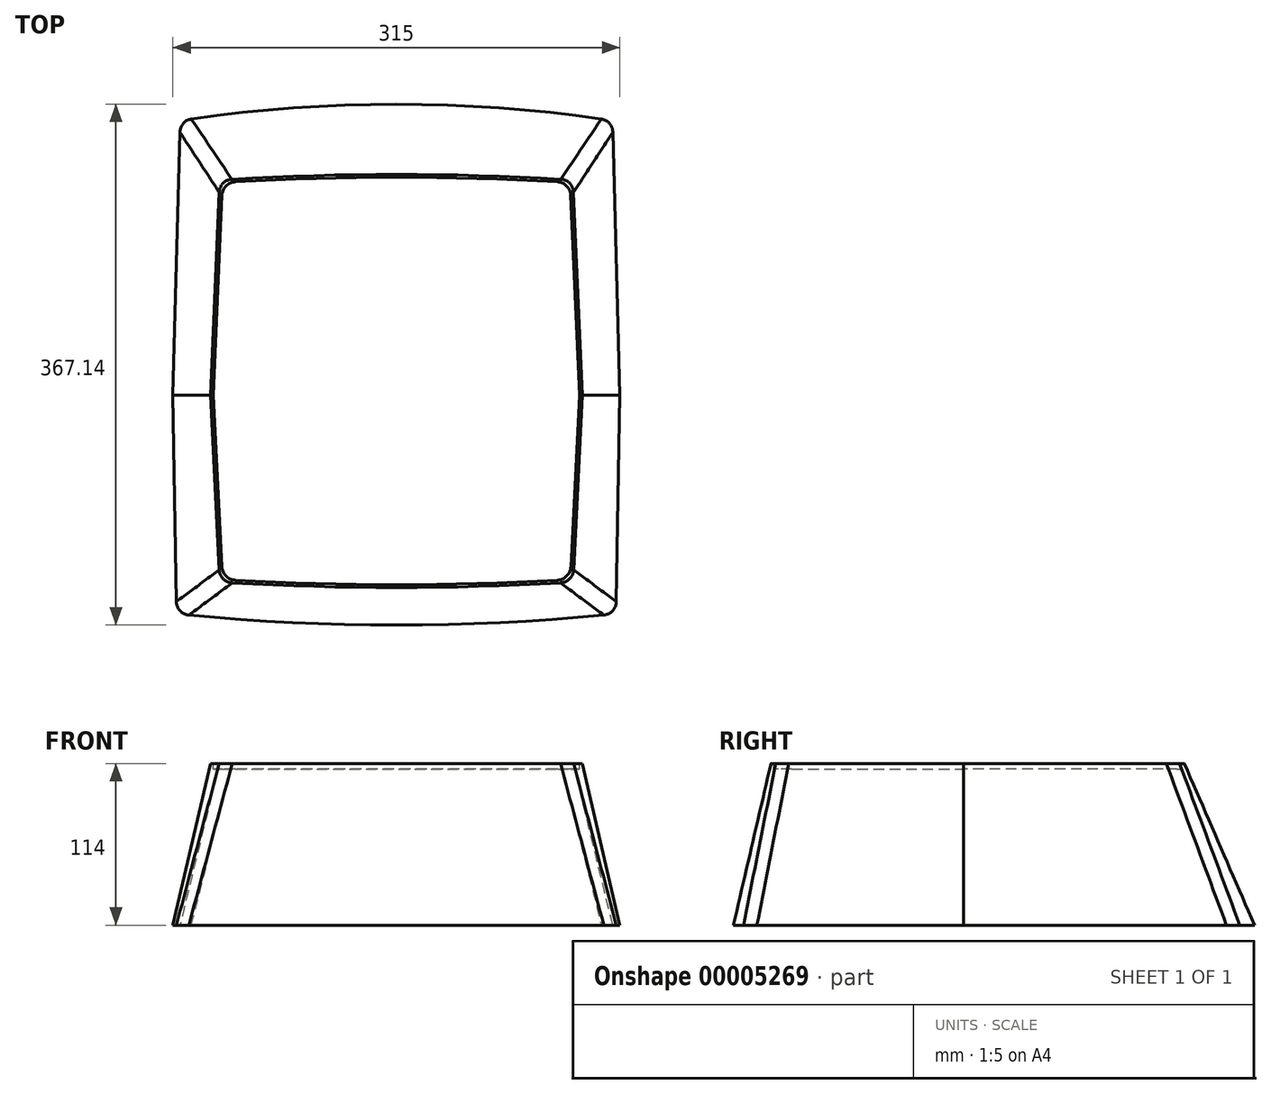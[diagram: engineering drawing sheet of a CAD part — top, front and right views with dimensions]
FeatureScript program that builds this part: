
annotation { "Feature Type Name" : "Feature", "Feature Type Description" : "" }
export const myFeature = defineFeature(function(context is Context, id is Id, definition is map)
    precondition{}
    {
        {
            var Q0;
            Q0=qCreatedBy(makeId("Top.planeOp"),FACE);
            var sketch = newSketch(context, id + "F0", { "sketchPlane" : qUnion([Q0])});
            skLineSegment(sketch, "E0", {"start": v(-157.5, 0) * mm, "end": v(-152.27, 193.54) * mm});
            skLineSegment(sketch, "E1", {"start": v(-152.27, 193.54) * mm, "end": v(152.27, 193.54) * mm, "construction": true});
            skLineSegment(sketch, "E2", {"start": v(152.27, 193.54) * mm, "end": v(157.5, 0) * mm});
            skLineSegment(sketch, "E3", {"start": v(157.5, 0) * mm, "end": v(154.85, -154.1) * mm});
            skLineSegment(sketch, "E4", {"start": v(154.85, -154.1) * mm, "end": v(-154.84, -154.1) * mm, "construction": true});
            skLineSegment(sketch, "E5", {"start": v(-154.84, -154.1) * mm, "end": v(-157.5, 0) * mm});
            skArc(sketch, "E6", {"start": v(152.27, 193.54) * mm, "mid": v(0, 205.09) * mm, "end": v(-152.27, 193.54) * mm});
            skArc(sketch, "E7", {"start": v(-154.84, -154.1) * mm, "mid": v(0, -162.05) * mm, "end": v(154.85, -154.1) * mm});
            skLineSegment(sketch, "E8", {"start": v(-157.5, 0) * mm, "end": v(157.5, 0) * mm, "construction": true});
            skPoint(sketch, "E9", {"position": v(0, 0) * mm});
            skPoint(sketch, "E10", {"position": v(0, 193.54) * mm});
            skPoint(sketch, "E11", {"position": v(0, -154.1) * mm});
            skSolve(sketch);
        }
        {
            var Q0;
            Q0=qCreatedBy(makeId("Top.planeOp"),FACE);
            cPlane(context, id + "F1", {"entities" : qUnion([Q0]), "cplaneType" : CPlaneType.OFFSET, "offset" : 114 * mm, "width" : 150 * mm, "height" : 150 * mm});
        }
        {
            var Q0;
            Q0=qCreatedBy(id+"F1.planeOp",FACE);
            var sketch = newSketch(context, id + "F2", { "sketchPlane" : qUnion([Q0])});
            skLineSegment(sketch, "E12", {"start": v(-129, 0) * mm, "end": v(-122.5, 149.86) * mm, "construction": true});
            skLineSegment(sketch, "E13", {"start": v(-122.5, 149.86) * mm, "end": v(122.5, 149.86) * mm, "construction": true});
            skLineSegment(sketch, "E14", {"start": v(122.5, 149.86) * mm, "end": v(129, 0) * mm, "construction": true});
            skLineSegment(sketch, "E15", {"start": v(129, 0) * mm, "end": v(122.5, -129.84) * mm, "construction": true});
            skLineSegment(sketch, "E16", {"start": v(122.5, -129.84) * mm, "end": v(-122.5, -129.84) * mm, "construction": true});
            skLineSegment(sketch, "E17", {"start": v(-122.5, -129.84) * mm, "end": v(-129, 0) * mm, "construction": true});
            skArc(sketch, "E18", {"start": v(122.5, 149.86) * mm, "mid": v(0, 153.61) * mm, "end": v(-122.5, 149.86) * mm, "construction": true});
            skArc(sketch, "E19", {"start": v(-122.5, -129.84) * mm, "mid": v(0, -133.6) * mm, "end": v(122.5, -129.84) * mm, "construction": true});
            skLineSegment(sketch, "E20", {"start": v(-129, 0) * mm, "end": v(129, 0) * mm, "construction": true});
            skPoint(sketch, "E21", {"position": v(0, 149.86) * mm});
            skPoint(sketch, "E22", {"position": v(0, -129.84) * mm});
            skPoint(sketch, "E23", {"position": v(0, 0) * mm});
            skLineSegment(sketch, "E24.0", {"start": v(-131, 0) * mm, "end": v(-124.42, 151.74) * mm});
            skLineSegment(sketch, "E24.1", {"start": v(-124.4, -131.72) * mm, "end": v(-131, 0) * mm});
            skArc(sketch, "E24.2", {"start": v(-124.4, -131.72) * mm, "mid": v(0, -135.6) * mm, "end": v(124.4, -131.72) * mm});
            skLineSegment(sketch, "E24.3", {"start": v(131, 0) * mm, "end": v(124.4, -131.72) * mm});
            skLineSegment(sketch, "E24.4", {"start": v(124.42, 151.74) * mm, "end": v(131, 0) * mm});
            skArc(sketch, "E24.5", {"start": v(124.42, 151.74) * mm, "mid": v(0, 155.61) * mm, "end": v(-124.42, 151.74) * mm});
            skSolve(sketch);
        }
        {
            var Q0;
            Q0=makeQuery(id+"F0.imprint","IMPRINT",FACE,{"disambiguationData":[TD([[makeQuery(id+"F0.imprint","IMPRINT",EDGE,{"derivedFrom":sQuery(id+"F0.wireOp",EDGE,"E0")}),-1.0]])]});
            var Q1;
            Q1=makeQuery(id+"F2.imprint","IMPRINT",FACE,{"disambiguationData":[TD([[makeQuery(id+"F2.imprint","IMPRINT",EDGE,{"derivedFrom":sQuery(id+"F2.wireOp",EDGE,"E24.0")}),-1.0]])]});
            loft(context, id + "F3", {"sheetProfilesArray" : [{ "sheetProfileEntities" : qUnion([Q0]) }, { "sheetProfileEntities" : qUnion([Q1]) }]});
        }
        {
            var Q0;
            Q0=makeQuery(id+"F2.imprint","IMPRINT",FACE,{"disambiguationData":[TD([[makeQuery(id+"F2.imprint","IMPRINT",EDGE,{"derivedFrom":sQuery(id+"F2.wireOp",EDGE,"E24.0")}),-1.0]])]});
            var sketch = newSketch(context, id + "F4", { "sketchPlane" : qUnion([Q0])});
            skArc(sketch, "E25.0", {"start": v(122.5, 149.86) * mm, "mid": v(0, 153.61) * mm, "end": v(-122.5, 149.86) * mm});
            skLineSegment(sketch, "E25.1", {"start": v(-129, 0) * mm, "end": v(-122.5, 149.86) * mm});
            skLineSegment(sketch, "E25.2", {"start": v(-122.5, -129.84) * mm, "end": v(-129, 0) * mm});
            skLineSegment(sketch, "E25.3", {"start": v(129, 0) * mm, "end": v(122.5, -129.84) * mm});
            skLineSegment(sketch, "E25.4", {"start": v(122.5, 149.86) * mm, "end": v(129, 0) * mm});
            skArc(sketch, "E25.5", {"start": v(-122.5, -129.84) * mm, "mid": v(0, -133.6) * mm, "end": v(122.5, -129.84) * mm});
            skSolve(sketch);
        }
        {
            var Q0;
            Q0=makeQuery(id+"F4.imprint","IMPRINT",FACE,{"disambiguationData":[TD([[makeQuery(id+"F4.imprint","IMPRINT",EDGE,{"derivedFrom":sQuery(id+"F4.wireOp",EDGE,"E25.0")}),1.0]])]});
            extrude(context, id + "F5", {"entities" : qUnion([Q0]), "operationType" : NewBodyOperationType.REMOVE, "oppositeDirection" : true, "depth" : 4 * mm});
        }
        {
            var Q0;
            Q0=makeQuery(id+"F3.opLoft","SWEPT_EDGE",EDGE,{"disambiguationData":[OSD([sQuery(id+"F0.wireOp",EDGE,"E5"),sQuery(id+"F0.wireOp",EDGE,"E7"),sQuery(id+"F2.wireOp",EDGE,"E24.1"),sQuery(id+"F2.wireOp",EDGE,"E24.2")])]});
            var Q1;
            Q1=makeQuery(id+"F5.boolean.opBoolean","COPY",EDGE,{"derivedFrom":makeQuery(id+"F5.opExtrude","SWEPT_EDGE",EDGE,{"disambiguationData":[OSD([sQuery(id+"F4.wireOp",EDGE,"E25.2"),sQuery(id+"F4.wireOp",EDGE,"E25.5")])]})});
            var Q2;
            Q2=makeQuery(id+"F5.boolean.opBoolean","COPY",EDGE,{"derivedFrom":makeQuery(id+"F5.opExtrude","SWEPT_EDGE",EDGE,{"disambiguationData":[OSD([sQuery(id+"F4.wireOp",EDGE,"E25.3"),sQuery(id+"F4.wireOp",EDGE,"E25.5")])]})});
            var Q3;
            Q3=makeQuery(id+"F5.boolean.opBoolean","COPY",EDGE,{"derivedFrom":makeQuery(id+"F5.opExtrude","SWEPT_EDGE",EDGE,{"disambiguationData":[OSD([sQuery(id+"F4.wireOp",EDGE,"E25.0"),sQuery(id+"F4.wireOp",EDGE,"E25.4")])]})});
            var Q4;
            Q4=makeQuery(id+"F5.boolean.opBoolean","COPY",EDGE,{"derivedFrom":makeQuery(id+"F5.opExtrude","SWEPT_EDGE",EDGE,{"disambiguationData":[OSD([sQuery(id+"F4.wireOp",EDGE,"E25.0"),sQuery(id+"F4.wireOp",EDGE,"E25.1")])]})});
            var Q5;
            Q5=makeQuery(id+"F3.opLoft","SWEPT_EDGE",EDGE,{"disambiguationData":[OSD([sQuery(id+"F0.wireOp",EDGE,"E2"),sQuery(id+"F0.wireOp",EDGE,"E6"),sQuery(id+"F2.wireOp",EDGE,"E24.4"),sQuery(id+"F2.wireOp",EDGE,"E24.5")])]});
            var Q6;
            Q6=makeQuery(id+"F3.opLoft","SWEPT_EDGE",EDGE,{"disambiguationData":[OSD([sQuery(id+"F0.wireOp",EDGE,"E3"),sQuery(id+"F0.wireOp",EDGE,"E7"),sQuery(id+"F2.wireOp",EDGE,"E24.2"),sQuery(id+"F2.wireOp",EDGE,"E24.3")])]});
            var Q7;
            Q7=makeQuery(id+"F3.opLoft","SWEPT_EDGE",EDGE,{"disambiguationData":[OSD([sQuery(id+"F0.wireOp",EDGE,"E0"),sQuery(id+"F0.wireOp",EDGE,"E6"),sQuery(id+"F2.wireOp",EDGE,"E24.0"),sQuery(id+"F2.wireOp",EDGE,"E24.5")])]});
            fillet(context, id + "F6", {"entities" : qUnion([Q0, Q1, Q2, Q3, Q4, Q5, Q6, Q7]), "radius" : 10 * mm, "tangentPropagation" : true, "allowEdgeOverflow" : false});
        }
    });
